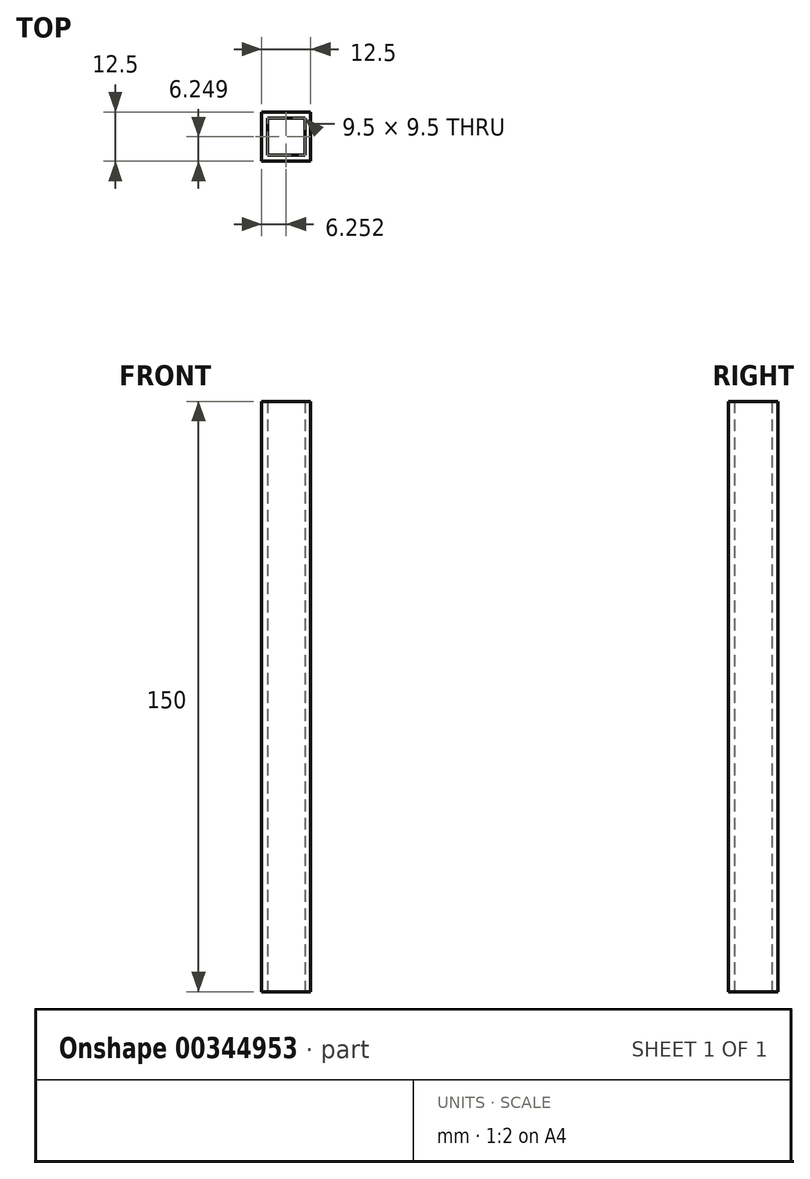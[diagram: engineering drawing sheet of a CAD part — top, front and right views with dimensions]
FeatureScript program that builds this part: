
annotation { "Feature Type Name" : "Feature", "Feature Type Description" : "" }
export const myFeature = defineFeature(function(context is Context, id is Id, definition is map)
    precondition{}
    {
        {
            var Q0;
            Q0=qCreatedBy(makeId("Top.planeOp"),FACE);
            var sketch = newSketch(context, id + "F0", { "sketchPlane" : qUnion([Q0])});
            skLineSegment(sketch, "E0.bottom", {"start": v(-6.2, 6.54) * mm, "end": v(3.3, 6.54) * mm});
            skLineSegment(sketch, "E0.top", {"start": v(-6.2, -2.96) * mm, "end": v(3.3, -2.96) * mm});
            skLineSegment(sketch, "E0.left", {"start": v(-6.2, 6.54) * mm, "end": v(-6.2, -2.96) * mm});
            skLineSegment(sketch, "E0.right", {"start": v(3.3, 6.54) * mm, "end": v(3.3, -2.96) * mm});
            skLineSegment(sketch, "E1.0", {"start": v(-7.7, 8.04) * mm, "end": v(4.8, 8.04) * mm});
            skLineSegment(sketch, "E1.1", {"start": v(-7.7, 8.04) * mm, "end": v(-7.7, -4.46) * mm});
            skLineSegment(sketch, "E1.2", {"start": v(-7.7, -4.46) * mm, "end": v(4.8, -4.46) * mm});
            skLineSegment(sketch, "E1.3", {"start": v(4.8, 8.04) * mm, "end": v(4.8, -4.46) * mm});
            skSolve(sketch);
        }
        {
            var Q0;
            Q0 = qSketchRegion(id + "F0", true);
            extrude(context, id + "F1", {"entities" : qUnion([Q0]), "flatOperationType" : FlatOperationType.REMOVE, "depth" : 150 * mm, "offsetDistance" : 25 * mm, "domain" : OperationDomain.MODEL});
        }
    });
